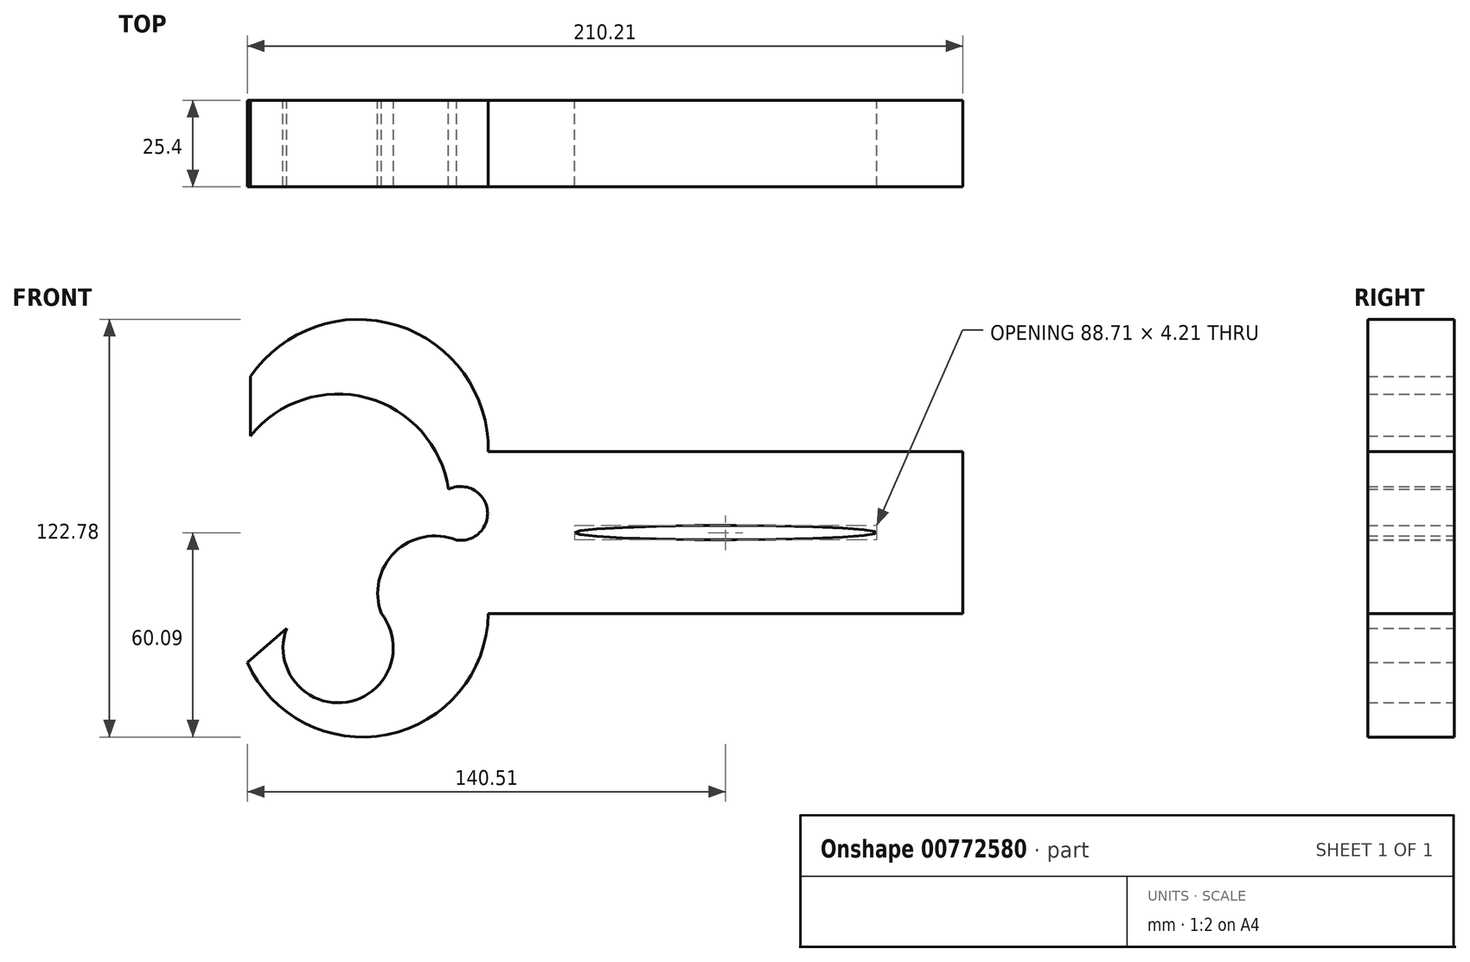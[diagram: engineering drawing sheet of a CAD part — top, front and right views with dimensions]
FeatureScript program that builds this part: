
annotation { "Feature Type Name" : "Feature", "Feature Type Description" : "" }
export const myFeature = defineFeature(function(context is Context, id is Id, definition is map)
    precondition{}
    {
        {
            var Q0;
            Q0=qCreatedBy(makeId("Front.planeOp"),FACE);
            var sketch = newSketch(context, id + "F0", { "sketchPlane" : qUnion([Q0])});
            skLineSegment(sketch, "E0.bottom", {"start": v(-69.7, -23.82) * mm, "end": v(69.7, -23.82) * mm});
            skLineSegment(sketch, "E0.top", {"start": v(-69.7, 23.82) * mm, "end": v(69.7, 23.82) * mm});
            skLineSegment(sketch, "E0.right", {"start": v(69.7, -23.82) * mm, "end": v(69.7, 23.82) * mm});
            skPoint(sketch, "E0.middle", {"position": v(0, 0) * mm});
            skEllipse(sketch, "E1", {"center": v(0, 0) * mm, "majorRadius": 44.35 * mm, "minorRadius": 2.1 * mm, "majorAxis": v(-1, 0)});
            skArc(sketch, "E2", {"start": v(-69.7, 23.82) * mm, "mid": v(-96.4, 60.92) * mm, "end": v(-139.55, 45.88) * mm});
            skLineSegment(sketch, "E3", {"start": v(-139.55, 45.88) * mm, "end": v(-139.55, 28.45) * mm});
            skArc(sketch, "E4", {"start": v(-81.42, 12.73) * mm, "mid": v(-105.34, 39.62) * mm, "end": v(-139.55, 28.45) * mm});
            skArc(sketch, "E5", {"start": v(-140.51, -38.2) * mm, "mid": v(-99.36, -59.35) * mm, "end": v(-69.7, -23.82) * mm});
            skLineSegment(sketch, "E6", {"start": v(-140.51, -38.2) * mm, "end": v(-128.98, -28.1) * mm});
            skArc(sketch, "E7", {"start": v(-128.98, -28.1) * mm, "mid": v(-111.35, -49.81) * mm, "end": v(-101.12, -23.78) * mm});
            skArc(sketch, "E8", {"start": v(-69.7, -23.82) * mm, "mid": v(-85.38, -0.93) * mm, "end": v(-101.12, -23.78) * mm});
            skArc(sketch, "E9", {"start": v(-81.42, -1.4) * mm, "mid": v(-69.93, 5.66) * mm, "end": v(-81.42, 12.73) * mm});
            skSolve(sketch);
        }
        {
            var Q0;
            Q0 = qSketchRegion(id + "F0", true);
            extrude(context, id + "F1", {"entities" : qUnion([Q0]), "depth" : 25.4 * mm, "offsetDistance" : 25.4 * mm});
        }
        {
            var Q0;
            Q0 = qSketchRegion(id + "F0", true);
            extrude(context, id + "F2", {"entities" : qUnion([Q0]), "operationType" : NewBodyOperationType.ADD, "depth" : 25.4 * mm, "offsetDistance" : 25.4 * mm});
        }
    });
